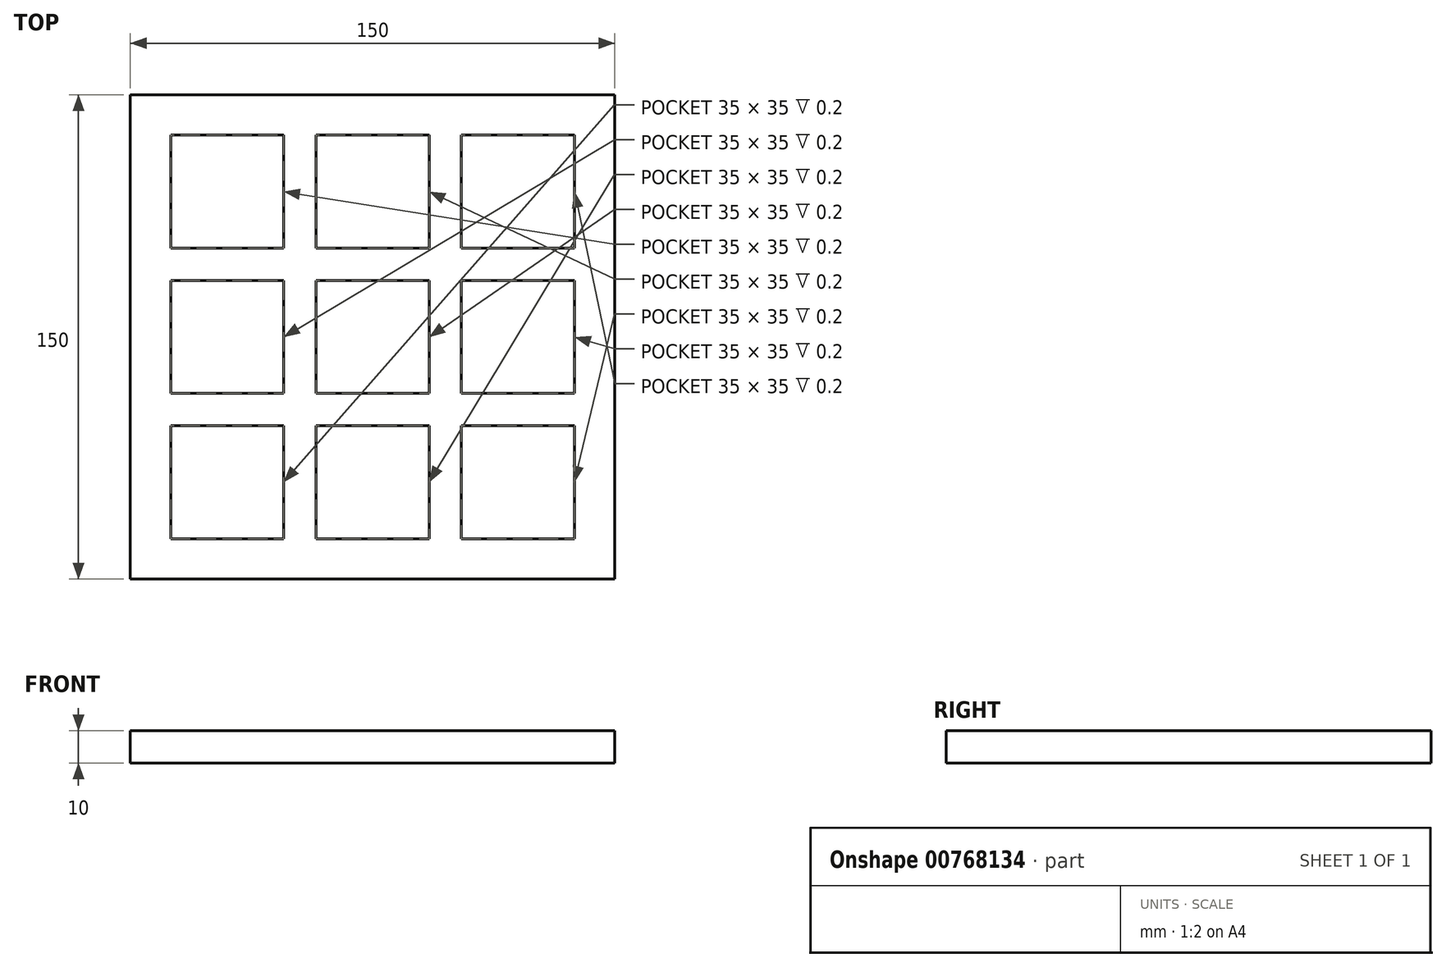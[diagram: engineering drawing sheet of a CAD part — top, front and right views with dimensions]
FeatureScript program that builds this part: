
annotation { "Feature Type Name" : "Feature", "Feature Type Description" : "" }
export const myFeature = defineFeature(function(context is Context, id is Id, definition is map)
    precondition{}
    {
        {
            var Q0;
            Q0=qCreatedBy(makeId("Top.planeOp"),FACE);
            var sketch = newSketch(context, id + "F0", { "sketchPlane" : qUnion([Q0])});
            skLineSegment(sketch, "E0.bottom", {"start": v(75, 75) * mm, "end": v(-75, 75) * mm});
            skLineSegment(sketch, "E0.top", {"start": v(75, -75) * mm, "end": v(-75, -75) * mm});
            skLineSegment(sketch, "E0.left", {"start": v(75, 75) * mm, "end": v(75, -75) * mm});
            skLineSegment(sketch, "E0.right", {"start": v(-75, 75) * mm, "end": v(-75, -75) * mm});
            skPoint(sketch, "E0.middle", {"position": v(0, 0) * mm});
            skLineSegment(sketch, "E1.bottom", {"start": v(-27.5, -27.5) * mm, "end": v(-62.5, -27.5) * mm});
            skLineSegment(sketch, "E1.top", {"start": v(-27.5, -62.5) * mm, "end": v(-62.5, -62.5) * mm});
            skLineSegment(sketch, "E1.left", {"start": v(-27.5, -27.5) * mm, "end": v(-27.5, -62.5) * mm});
            skLineSegment(sketch, "E1.right", {"start": v(-62.5, -27.5) * mm, "end": v(-62.5, -62.5) * mm});
            skPoint(sketch, "E1.middle", {"position": v(-45, -45) * mm});
            skLineSegment(sketch, "E2.0.1.0", {"start": v(-27.5, 17.5) * mm, "end": v(-62.5, 17.5) * mm});
            skLineSegment(sketch, "E2.0.1.1", {"start": v(-27.5, 17.5) * mm, "end": v(-27.5, -17.5) * mm});
            skLineSegment(sketch, "E2.0.1.2", {"start": v(-27.5, -17.5) * mm, "end": v(-62.5, -17.5) * mm});
            skLineSegment(sketch, "E2.0.1.3", {"start": v(-62.5, 17.5) * mm, "end": v(-62.5, -17.5) * mm});
            skLineSegment(sketch, "E2.1.0.0", {"start": v(17.5, -27.5) * mm, "end": v(-17.5, -27.5) * mm});
            skLineSegment(sketch, "E2.1.0.1", {"start": v(17.5, -27.5) * mm, "end": v(17.5, -62.5) * mm});
            skLineSegment(sketch, "E2.1.0.2", {"start": v(17.5, -62.5) * mm, "end": v(-17.5, -62.5) * mm});
            skLineSegment(sketch, "E2.1.0.3", {"start": v(-17.5, -27.5) * mm, "end": v(-17.5, -62.5) * mm});
            skLineSegment(sketch, "E2.1.1.0", {"start": v(17.5, 17.5) * mm, "end": v(-17.5, 17.5) * mm});
            skLineSegment(sketch, "E2.1.1.1", {"start": v(17.5, 17.5) * mm, "end": v(17.5, -17.5) * mm});
            skLineSegment(sketch, "E2.1.1.2", {"start": v(17.5, -17.5) * mm, "end": v(-17.5, -17.5) * mm});
            skLineSegment(sketch, "E2.1.1.3", {"start": v(-17.5, 17.5) * mm, "end": v(-17.5, -17.5) * mm});
            skLineSegment(sketch, "E2.direction1", {"start": v(-62.5, -62.5) * mm, "end": v(-17.5, -62.5) * mm, "construction": true});
            skLineSegment(sketch, "E2.direction2", {"start": v(-62.5, -62.5) * mm, "end": v(-62.5, -17.5) * mm, "construction": true});
            skLineSegment(sketch, "E3.0.0.2", {"start": v(-27.5, 62.5) * mm, "end": v(-62.5, 62.5) * mm});
            skLineSegment(sketch, "E3.3.0.2", {"start": v(-27.5, 62.5) * mm, "end": v(-27.5, 27.5) * mm});
            skLineSegment(sketch, "E3.6.0.2", {"start": v(-27.5, 27.5) * mm, "end": v(-62.5, 27.5) * mm});
            skLineSegment(sketch, "E3.9.0.2", {"start": v(-62.5, 62.5) * mm, "end": v(-62.5, 27.5) * mm});
            skLineSegment(sketch, "E3.0.1.2", {"start": v(17.5, 62.5) * mm, "end": v(-17.5, 62.5) * mm});
            skLineSegment(sketch, "E3.3.1.2", {"start": v(17.5, 62.5) * mm, "end": v(17.5, 27.5) * mm});
            skLineSegment(sketch, "E3.6.1.2", {"start": v(17.5, 27.5) * mm, "end": v(-17.5, 27.5) * mm});
            skLineSegment(sketch, "E3.9.1.2", {"start": v(-17.5, 62.5) * mm, "end": v(-17.5, 27.5) * mm});
            skLineSegment(sketch, "E4.0.2.0", {"start": v(62.5, -27.5) * mm, "end": v(27.5, -27.5) * mm});
            skLineSegment(sketch, "E4.3.2.0", {"start": v(62.5, -27.5) * mm, "end": v(62.5, -62.5) * mm});
            skLineSegment(sketch, "E4.6.2.0", {"start": v(62.5, -62.5) * mm, "end": v(27.5, -62.5) * mm});
            skLineSegment(sketch, "E4.9.2.0", {"start": v(27.5, -27.5) * mm, "end": v(27.5, -62.5) * mm});
            skLineSegment(sketch, "E4.0.2.1", {"start": v(62.5, 17.5) * mm, "end": v(27.5, 17.5) * mm});
            skLineSegment(sketch, "E4.3.2.1", {"start": v(62.5, 17.5) * mm, "end": v(62.5, -17.5) * mm});
            skLineSegment(sketch, "E4.6.2.1", {"start": v(62.5, -17.5) * mm, "end": v(27.5, -17.5) * mm});
            skLineSegment(sketch, "E4.9.2.1", {"start": v(27.5, 17.5) * mm, "end": v(27.5, -17.5) * mm});
            skLineSegment(sketch, "E4.0.2.2", {"start": v(62.5, 62.5) * mm, "end": v(27.5, 62.5) * mm});
            skLineSegment(sketch, "E4.3.2.2", {"start": v(62.5, 62.5) * mm, "end": v(62.5, 27.5) * mm});
            skLineSegment(sketch, "E4.6.2.2", {"start": v(62.5, 27.5) * mm, "end": v(27.5, 27.5) * mm});
            skLineSegment(sketch, "E4.9.2.2", {"start": v(27.5, 62.5) * mm, "end": v(27.5, 27.5) * mm});
            skSolve(sketch);
        }
        {
            var Q0;
            Q0=makeQuery(id+"F0.imprint","IMPRINT",FACE,{"disambiguationData":[TD([[makeQuery(id+"F0.imprint","IMPRINT",EDGE,{"derivedFrom":sQuery(id+"F0.wireOp",EDGE,"E0.bottom")}),1.0]])]});
            extrude(context, id + "F1", {"entities" : qUnion([Q0]), "depth" : 10 * mm, "offsetDistance" : 25 * mm});
        }
        {
            var Q0;
            Q0=makeQuery(id+"F0.imprint","IMPRINT",FACE,{"disambiguationData":[TD([[makeQuery(id+"F0.imprint","IMPRINT",EDGE,{"derivedFrom":sQuery(id+"F0.wireOp",EDGE,"E3.0.0.2")}),1.0]])]});
            var Q1;
            Q1=makeQuery(id+"F0.imprint","IMPRINT",FACE,{"disambiguationData":[TD([[makeQuery(id+"F0.imprint","IMPRINT",EDGE,{"derivedFrom":sQuery(id+"F0.wireOp",EDGE,"E2.0.1.0")}),1.0]])]});
            var Q2;
            Q2=makeQuery(id+"F0.imprint","IMPRINT",FACE,{"disambiguationData":[TD([[makeQuery(id+"F0.imprint","IMPRINT",EDGE,{"derivedFrom":sQuery(id+"F0.wireOp",EDGE,"E1.bottom")}),1.0]])]});
            var Q3;
            Q3=makeQuery(id+"F0.imprint","IMPRINT",FACE,{"disambiguationData":[TD([[makeQuery(id+"F0.imprint","IMPRINT",EDGE,{"derivedFrom":sQuery(id+"F0.wireOp",EDGE,"E2.1.0.0")}),1.0]])]});
            var Q4;
            Q4=makeQuery(id+"F0.imprint","IMPRINT",FACE,{"disambiguationData":[TD([[makeQuery(id+"F0.imprint","IMPRINT",EDGE,{"derivedFrom":sQuery(id+"F0.wireOp",EDGE,"E2.1.1.0")}),1.0]])]});
            var Q5;
            Q5=makeQuery(id+"F0.imprint","IMPRINT",FACE,{"disambiguationData":[TD([[makeQuery(id+"F0.imprint","IMPRINT",EDGE,{"derivedFrom":sQuery(id+"F0.wireOp",EDGE,"E3.0.1.2")}),1.0]])]});
            var Q6;
            Q6=makeQuery(id+"F0.imprint","IMPRINT",FACE,{"disambiguationData":[TD([[makeQuery(id+"F0.imprint","IMPRINT",EDGE,{"derivedFrom":sQuery(id+"F0.wireOp",EDGE,"E4.0.2.2")}),1.0]])]});
            var Q7;
            Q7=makeQuery(id+"F0.imprint","IMPRINT",FACE,{"disambiguationData":[TD([[makeQuery(id+"F0.imprint","IMPRINT",EDGE,{"derivedFrom":sQuery(id+"F0.wireOp",EDGE,"E4.0.2.1")}),1.0]])]});
            var Q8;
            Q8=makeQuery(id+"F0.imprint","IMPRINT",FACE,{"disambiguationData":[TD([[makeQuery(id+"F0.imprint","IMPRINT",EDGE,{"derivedFrom":sQuery(id+"F0.wireOp",EDGE,"E4.0.2.0")}),1.0]])]});
            extrude(context, id + "F2", {"entities" : qUnion([Q0, Q1, Q2, Q3, Q4, Q5, Q6, Q7, Q8]), "operationType" : NewBodyOperationType.ADD, "depth" : 9.8 * mm, "offsetDistance" : 25 * mm});
        }
    });
